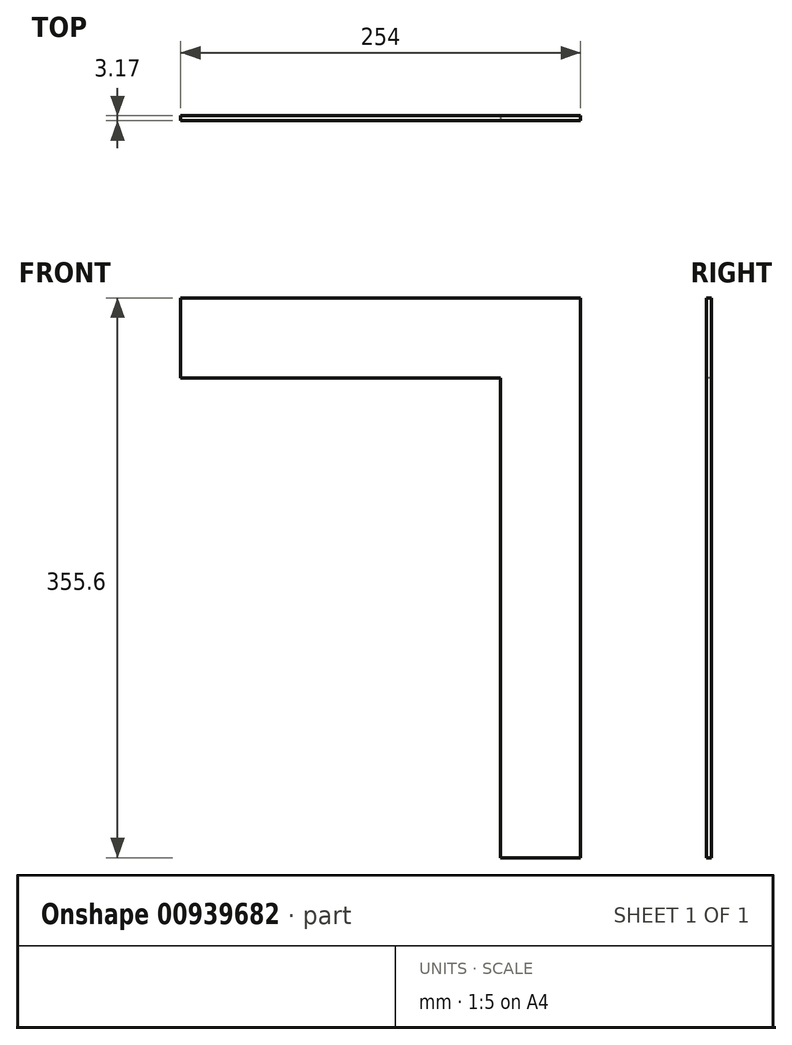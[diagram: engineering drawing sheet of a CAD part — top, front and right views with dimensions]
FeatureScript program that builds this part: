
annotation { "Feature Type Name" : "Feature", "Feature Type Description" : "" }
export const myFeature = defineFeature(function(context is Context, id is Id, definition is map)
    precondition{}
    {
        {
            var Q0;
            Q0=qCreatedBy(makeId("Front.planeOp"),FACE);
            var sketch = newSketch(context, id + "F0", { "sketchPlane" : qUnion([Q0])});
            skLineSegment(sketch, "E0.bottom", {"start": v(0, 0) * mm, "end": v(-50.8, 0) * mm});
            skLineSegment(sketch, "E0.top", {"start": v(0, 304.8) * mm, "end": v(-50.8, 304.8) * mm});
            skLineSegment(sketch, "E0.left", {"start": v(0, 0) * mm, "end": v(0, 304.8) * mm});
            skLineSegment(sketch, "E0.right", {"start": v(-50.8, 0) * mm, "end": v(-50.8, 304.8) * mm});
            skLineSegment(sketch, "E1.bottom", {"start": v(0, 304.8) * mm, "end": v(-254, 304.8) * mm});
            skLineSegment(sketch, "E1.top", {"start": v(0, 355.6) * mm, "end": v(-254, 355.6) * mm});
            skLineSegment(sketch, "E1.left", {"start": v(0, 304.8) * mm, "end": v(0, 355.6) * mm});
            skLineSegment(sketch, "E1.right", {"start": v(-254, 304.8) * mm, "end": v(-254, 355.6) * mm});
            skSolve(sketch);
        }
        {
            var Q0;
            Q0 = qSketchRegion(id + "F0", true);
            extrude(context, id + "F1", {"entities" : qUnion([Q0]), "oppositeDirection" : true, "depth" : 3.17 * mm, "offsetDistance" : 25.4 * mm});
        }
    });
